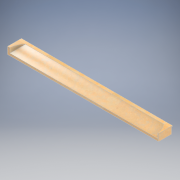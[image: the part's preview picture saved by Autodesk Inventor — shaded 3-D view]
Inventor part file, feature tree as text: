
AUTODESK INVENTOR PART (.ipt)
format: ipt  version: 2022.2 (Build 262287010, 287A)  size: 203,776 bytes
history: native  units: in
note: dims shown in document units (in); Inventor stores cm internally (conversion verified against a paired STEP export)
features: revolve x2, direct_edit x1, extrude x1, sketch x1, projected_geometry x1
ambient origin geometry x8: Origin, YZ Plane, XZ Plane, XY Plane, X Axis, Y Axis, Z Axis, Center Point
bodies: Solid1 (feature_tree), Body1 (feature_tree)
feature tree (6):
  direct_edit  "Direct Edit1"
  extrude  "Extrusion1"  [1 undecoded]
  sketch  "Sketch1"  dims[d0=180.0deg d1=-0.6184in d2=0.375in d3=0.0in]
  projected_geometry  "Projected Loop1"
  revolve  "Rotate1"  [1 undecoded]
  revolve  "Rotate2"  [1 undecoded]
note: 3 required parameter values undecoded (feature->parameter linkage not recoverable at this tier; creation-order binding heuristic only, values carry confidence <= 0.55)